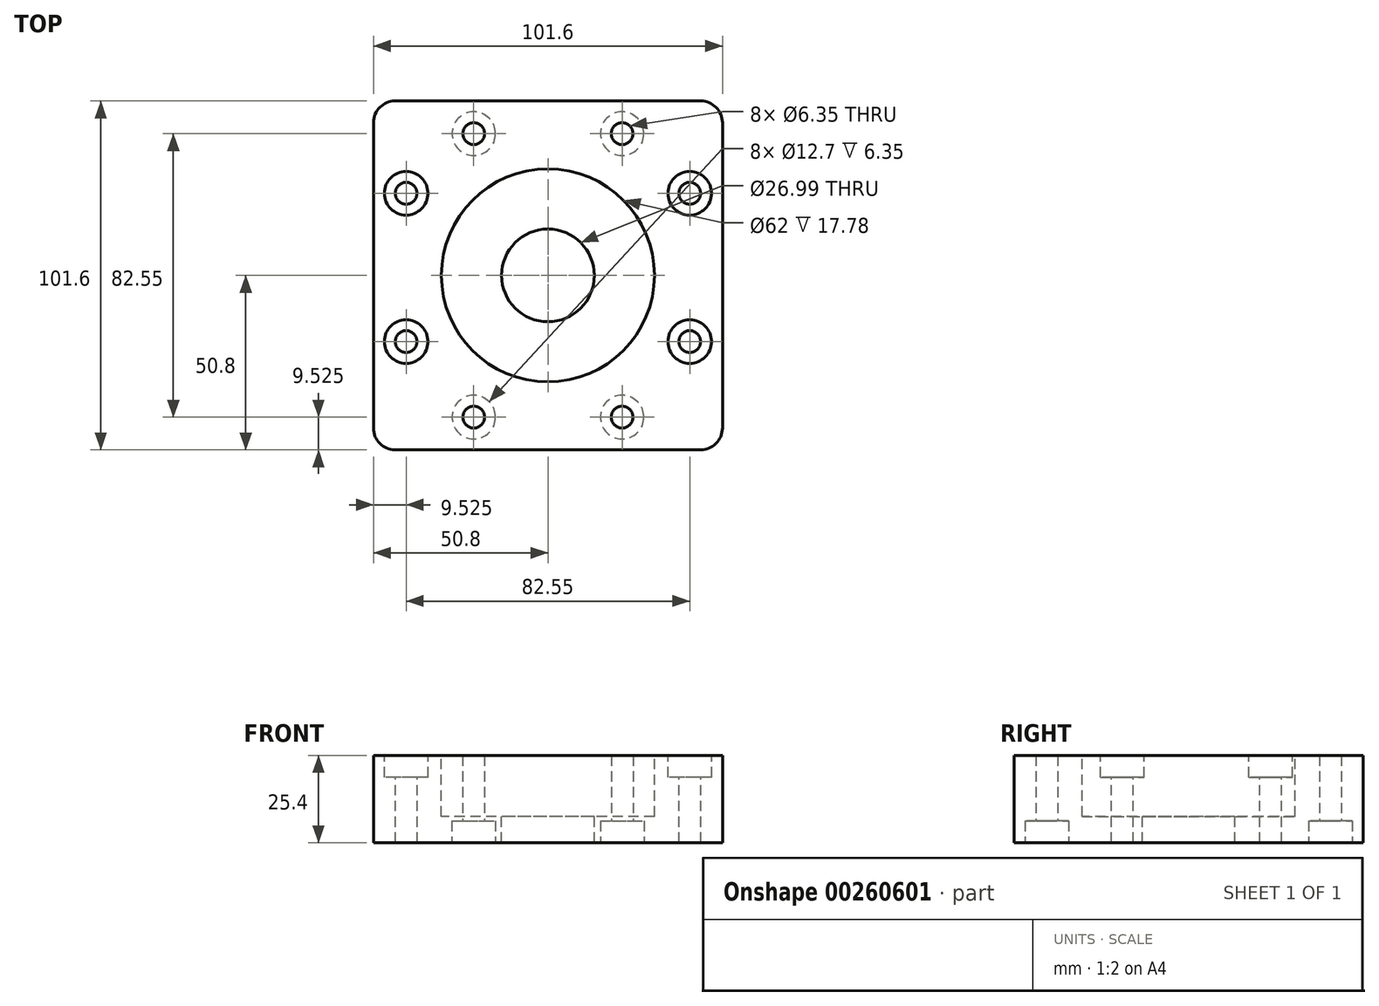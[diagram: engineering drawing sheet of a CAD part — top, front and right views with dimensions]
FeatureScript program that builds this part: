
annotation { "Feature Type Name" : "Feature", "Feature Type Description" : "" }
export const myFeature = defineFeature(function(context is Context, id is Id, definition is map)
    precondition{}
    {
        {
            var Q0;
            Q0=qCreatedBy(makeId("Top.planeOp"),FACE);
            var sketch = newSketch(context, id + "F0", { "sketchPlane" : qUnion([Q0])});
            skLineSegment(sketch, "E0.bottom", {"start": v(-44.45, -50.8) * mm, "end": v(44.45, -50.8) * mm});
            skLineSegment(sketch, "E0.top", {"start": v(-44.45, 50.8) * mm, "end": v(44.45, 50.8) * mm});
            skLineSegment(sketch, "E0.left", {"start": v(-50.8, -44.45) * mm, "end": v(-50.8, 44.45) * mm});
            skLineSegment(sketch, "E0.right", {"start": v(50.8, -44.45) * mm, "end": v(50.8, 44.45) * mm});
            skPoint(sketch, "E0.middle", {"position": v(0, 0) * mm});
            skPoint(sketch, "E1.visualSharp", {"position": v(-50.8, -50.8) * mm});
            skArc(sketch, "E1.filletArc", {"start": v(-50.8, -44.45) * mm, "mid": v(-48.94, -48.94) * mm, "end": v(-44.45, -50.8) * mm});
            skPoint(sketch, "E2.visualSharp", {"position": v(50.8, -50.8) * mm});
            skArc(sketch, "E2.filletArc", {"start": v(44.45, -50.8) * mm, "mid": v(48.94, -48.94) * mm, "end": v(50.8, -44.45) * mm});
            skPoint(sketch, "E3.visualSharp", {"position": v(50.8, 50.8) * mm});
            skArc(sketch, "E3.filletArc", {"start": v(50.8, 44.45) * mm, "mid": v(48.94, 48.94) * mm, "end": v(44.45, 50.8) * mm});
            skPoint(sketch, "E4.visualSharp", {"position": v(-50.8, 50.8) * mm});
            skArc(sketch, "E4.filletArc", {"start": v(-44.45, 50.8) * mm, "mid": v(-48.94, 48.94) * mm, "end": v(-50.8, 44.45) * mm});
            skLineSegment(sketch, "E5.bottom", {"start": v(-31.75, -50.8) * mm, "end": v(31.75, -50.8) * mm});
            skPoint(sketch, "E6", {"position": v(-21.6, 41.28) * mm});
            skPoint(sketch, "E7", {"position": v(21.59, 41.28) * mm});
            skPoint(sketch, "E8", {"position": v(-21.59, -41.28) * mm});
            skPoint(sketch, "E9", {"position": v(21.6, -41.28) * mm});
            skPoint(sketch, "E10", {"position": v(-41.27, -21.59) * mm});
            skPoint(sketch, "E11", {"position": v(-41.28, 21.6) * mm});
            skPoint(sketch, "E12", {"position": v(41.27, 21.6) * mm});
            skPoint(sketch, "E13", {"position": v(41.28, -21.59) * mm});
            skSolve(sketch);
        }
        {
            var Q0;
            Q0=makeQuery(id+"F0.imprint","IMPRINT",FACE,{"disambiguationData":[TD([[makeQuery(id+"F0.imprint","IMPRINT",EDGE,{"derivedFrom":sQuery(id+"F0.wireOp",EDGE,"E0.bottom")}),1.0]])]});
            extrude(context, id + "F1", {"entities" : qUnion([Q0]), "depth" : 25.4 * mm});
        }
        {
            var Q0;
            Q0=makeQuery(id+"F1.opExtrude","CAP_FACE",FACE,{"disambiguationData":[OSD([sQuery(id+"F0.wireOp",EDGE,"E0.bottom"),sQuery(id+"F0.wireOp",EDGE,"E0.top"),sQuery(id+"F0.wireOp",EDGE,"E0.left"),sQuery(id+"F0.wireOp",EDGE,"E0.right")])],"isStart":false});
            var sketch = newSketch(context, id + "F2", { "sketchPlane" : qUnion([Q0])});
            skCircle(sketch, "E14", {"center": v(0, 0) * mm, "radius": 13.5 * mm});
            skSolve(sketch);
        }
        {
            var Q0;
            Q0=makeQuery(id+"F2.imprint","IMPRINT",FACE,{"disambiguationData":[TD([[makeQuery(id+"F2.imprint","IMPRINT",EDGE,{"derivedFrom":sQuery(id+"F2.wireOp",EDGE,"E14")}),1.0]])]});
            extrude(context, id + "F3", {"entities" : qUnion([Q0]), "operationType" : NewBodyOperationType.REMOVE, "oppositeDirection" : true, "depth" : 25.4 * mm});
        }
        {
            var Q0;
            Q0=makeQuery(id+"F1.opExtrude","CAP_FACE",FACE,{"disambiguationData":[OSD([sQuery(id+"F0.wireOp",EDGE,"E0.bottom"),sQuery(id+"F0.wireOp",EDGE,"E0.top"),sQuery(id+"F0.wireOp",EDGE,"E0.left"),sQuery(id+"F0.wireOp",EDGE,"E0.right"),sQuery(id+"F0.wireOp",EDGE,"E1.filletArc"),sQuery(id+"F0.wireOp",EDGE,"E2.filletArc"),sQuery(id+"F0.wireOp",EDGE,"E3.filletArc"),sQuery(id+"F0.wireOp",EDGE,"E4.filletArc")])],"isStart":false});
            var sketch = newSketch(context, id + "F4", { "sketchPlane" : qUnion([Q0])});
            skCircle(sketch, "E15", {"center": v(0, 0) * mm, "radius": 31 * mm});
            skSolve(sketch);
        }
        {
            var Q0;
            Q0=makeQuery(id+"F4.imprint","IMPRINT",FACE,{"disambiguationData":[TD([[makeQuery(id+"F4.imprint","IMPRINT",EDGE,{"derivedFrom":sQuery(id+"F4.wireOp",EDGE,"E15")}),1.0]])]});
            extrude(context, id + "F5", {"entities" : qUnion([Q0]), "operationType" : NewBodyOperationType.REMOVE, "oppositeDirection" : true, "depth" : 17.78 * mm});
        }
        {
            var Q0;
            Q0=qCreatedBy(makeId("Top.planeOp"),FACE);
            var sketch = newSketch(context, id + "F6", { "sketchPlane" : qUnion([Q0])});
            skCircle(sketch, "E16", {"center": v(-113.8, 0) * mm, "radius": 12.5 * mm});
            skCircle(sketch, "E17", {"center": v(-113.8, 0) * mm, "radius": 31 * mm});
            skSolve(sketch);
        }
        {
            var Q0;
            Q0=makeQuery(id+"F6.imprint","IMPRINT",FACE,{"disambiguationData":[TD([[makeQuery(id+"F6.imprint","IMPRINT",EDGE,{"derivedFrom":sQuery(id+"F6.wireOp",EDGE,"E16")}),-1.0]])]});
            extrude(context, id + "F7", {"entities" : qUnion([Q0]), "depth" : 17 * mm});
        }
        {
            var Q0;
            Q0 = qSketchRegion(id + "F6", true);
            extrude(context, id + "F8", {"entities" : qUnion([Q0]), "depth" : 17 * mm});
        }
        {
            var Q0;
            Q0=makeQuery(id+"F7.opExtrude","SWEPT_BODY",BODY,{"disambiguationData":[OSD([sQuery(id+"F6.wireOp",EDGE,"E16"),sQuery(id+"F6.wireOp",EDGE,"E17")])]});
            deleteBodies(context, id + "F9", {"entities" : qUnion([Q0])});
        }
        {
            var Q0;
            Q0=makeQuery(id+"F8.opExtrude","SWEPT_BODY",BODY,{"disambiguationData":[OSD([sQuery(id+"F6.wireOp",EDGE,"E16"),sQuery(id+"F6.wireOp",EDGE,"E17")])]});
            deleteBodies(context, id + "F10", {"entities" : qUnion([Q0])});
        }
        {
            var Q0;
            Q0=sQuery(id+"F0.wireOp",VERTEX,"E6");
            var Q1;
            Q1=sQuery(id+"F0.wireOp",VERTEX,"E7");
            var Q2;
            Q2=sQuery(id+"F0.wireOp",VERTEX,"E8");
            var Q3;
            Q3=sQuery(id+"F0.wireOp",VERTEX,"E9");
            var Q4;
            Q4=sQuery(id+"F0.wireOp",VERTEX,"cf4996f7-e357-49bc-898a-85166dcc69ef");
            var Q5;
            Q5=sQuery(id+"F0.wireOp",VERTEX,"f223fe2a-1e97-4e2d-89e4-f0193a8c639e");
            var Q6;
            Q6=makeQuery(id+"F1.opExtrude","SWEPT_BODY",BODY,{"disambiguationData":[OSD([sQuery(id+"F0.wireOp",EDGE,"E0.bottom"),sQuery(id+"F0.wireOp",EDGE,"E0.top"),sQuery(id+"F0.wireOp",EDGE,"E0.left"),sQuery(id+"F0.wireOp",EDGE,"E0.right"),sQuery(id+"F0.wireOp",EDGE,"E1.filletArc"),sQuery(id+"F0.wireOp",EDGE,"E2.filletArc"),sQuery(id+"F0.wireOp",EDGE,"E3.filletArc"),sQuery(id+"F0.wireOp",EDGE,"E4.filletArc"),sQuery(id+"F0.wireOp",EDGE,"E5.bottom")])]});
            hole(context, id + "F11", {"style" : HoleStyle.C_BORE, "endStyle" : HoleEndStyle.BLIND, "oppositeDirection" : true, "holeDiameter" : 6.35 * mm, "cBoreDiameter" : 12.7 * mm, "cBoreDepth" : 6.35 * mm, "holeDepth" : 38.1 * mm, "tappedDepth" : 12.7 * mm, "tapClearance" : 3, "locations" : qUnion([Q0, Q1, Q2, Q3, Q4, Q5]), "scope" : qUnion([Q6])});
        }
        {
            var Q0;
            Q0=makeQuery(id+"F1.opExtrude","CAP_FACE",FACE,{"disambiguationData":[OSD([sQuery(id+"F0.wireOp",EDGE,"E0.bottom"),sQuery(id+"F0.wireOp",EDGE,"E0.top"),sQuery(id+"F0.wireOp",EDGE,"E0.left"),sQuery(id+"F0.wireOp",EDGE,"E0.right"),sQuery(id+"F0.wireOp",EDGE,"E1.filletArc"),sQuery(id+"F0.wireOp",EDGE,"E2.filletArc"),sQuery(id+"F0.wireOp",EDGE,"E3.filletArc"),sQuery(id+"F0.wireOp",EDGE,"E4.filletArc"),sQuery(id+"F0.wireOp",EDGE,"E5.bottom")])],"isStart":false});
            var sketch = newSketch(context, id + "F12", { "sketchPlane" : qUnion([Q0])});
            skPoint(sketch, "E18.middle", {"position": v(0, 0) * mm});
            skPoint(sketch, "E19", {"position": v(-41.28, -19.28) * mm});
            skPoint(sketch, "E20", {"position": v(-41.28, 23.9) * mm});
            skPoint(sketch, "E21", {"position": v(41.27, 23.9) * mm});
            skPoint(sketch, "E22", {"position": v(41.27, -19.28) * mm});
            skSolve(sketch);
        }
        {
            var Q0;
            Q0=sQuery(id+"F12.wireOp",VERTEX,"E20");
            var Q1;
            Q1=sQuery(id+"F12.wireOp",VERTEX,"E19");
            var Q2;
            Q2=sQuery(id+"F12.wireOp",VERTEX,"E21");
            var Q3;
            Q3=sQuery(id+"F12.wireOp",VERTEX,"E22");
            var Q4;
            Q4=makeQuery(id+"F1.opExtrude","SWEPT_BODY",BODY,{"disambiguationData":[OSD([sQuery(id+"F0.wireOp",EDGE,"E0.bottom"),sQuery(id+"F0.wireOp",EDGE,"E0.top"),sQuery(id+"F0.wireOp",EDGE,"E0.left"),sQuery(id+"F0.wireOp",EDGE,"E0.right"),sQuery(id+"F0.wireOp",EDGE,"E1.filletArc"),sQuery(id+"F0.wireOp",EDGE,"E2.filletArc"),sQuery(id+"F0.wireOp",EDGE,"E3.filletArc"),sQuery(id+"F0.wireOp",EDGE,"E4.filletArc"),sQuery(id+"F0.wireOp",EDGE,"E5.bottom")])]});
            hole(context, id + "F13", {"style" : HoleStyle.C_BORE, "endStyle" : HoleEndStyle.BLIND, "holeDiameter" : 6.35 * mm, "cBoreDiameter" : 12.7 * mm, "cBoreDepth" : 6.35 * mm, "holeDepth" : 38.1 * mm, "tappedDepth" : 12.7 * mm, "tapClearance" : 3, "locations" : qUnion([Q0, Q1, Q2, Q3]), "scope" : qUnion([Q4])});
        }
    });
